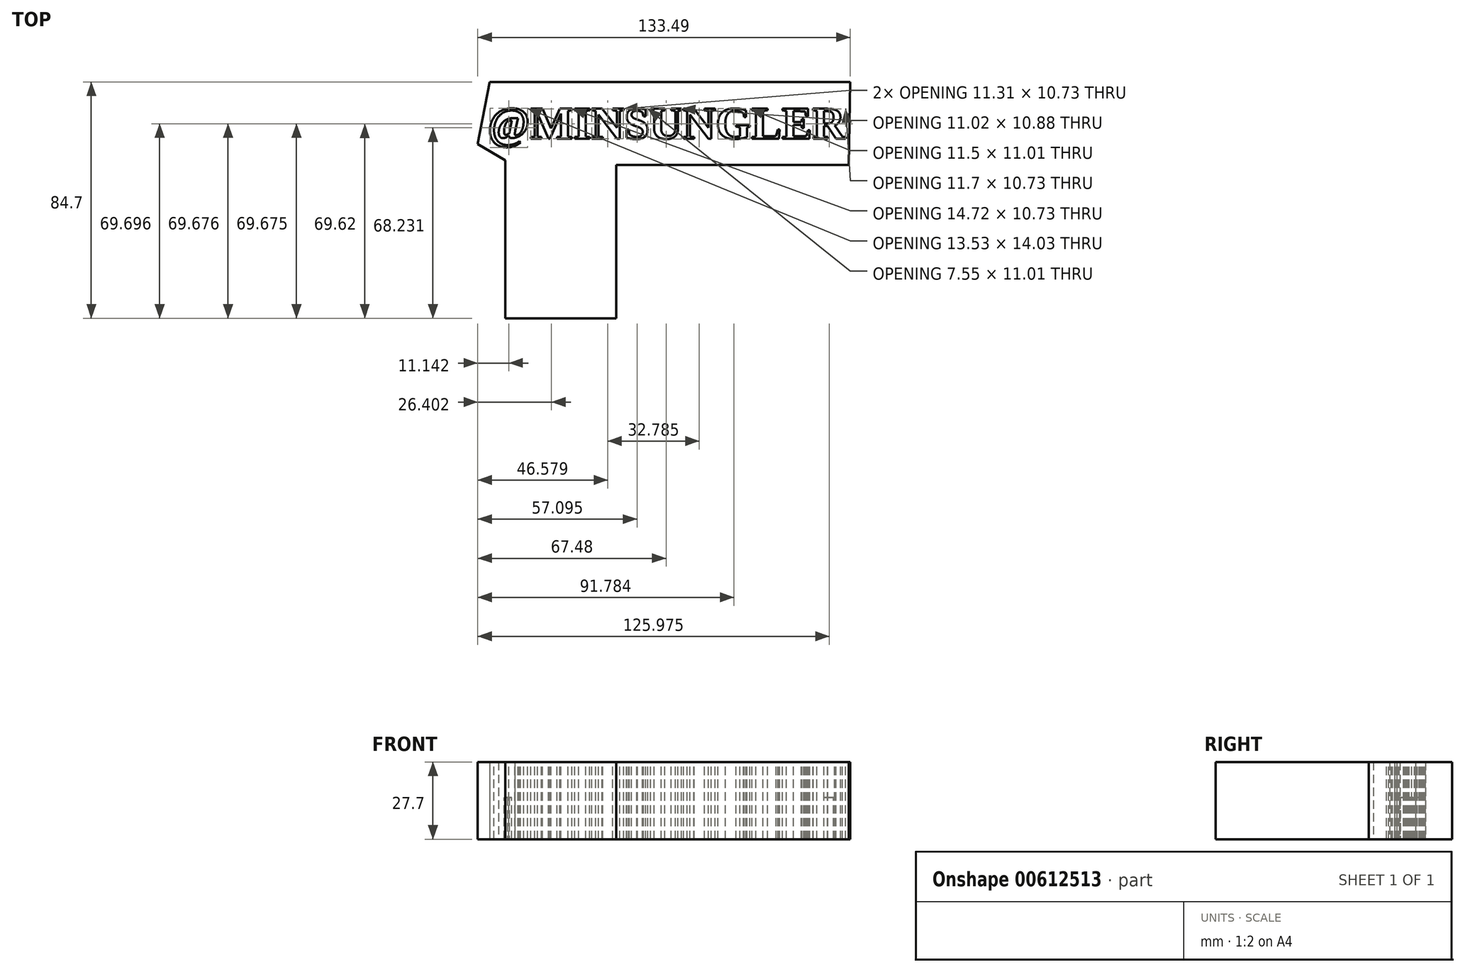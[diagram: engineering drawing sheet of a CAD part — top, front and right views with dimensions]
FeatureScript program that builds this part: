
annotation { "Feature Type Name" : "Feature", "Feature Type Description" : "" }
export const myFeature = defineFeature(function(context is Context, id is Id, definition is map)
    precondition{}
    {
        {
            var Q0;
            Q0=qCreatedBy(makeId("Top.planeOp"),FACE);
            var sketch = newSketch(context, id + "F0", { "sketchPlane" : qUnion([Q0])});
            skLineSegment(sketch, "E0", {"start": v(76.26, 48.78) * mm, "end": v(-52.94, 48.78) * mm});
            skLineSegment(sketch, "E1", {"start": v(-52.94, 48.78) * mm, "end": v(-57.23, 26.54) * mm});
            skLineSegment(sketch, "E2", {"start": v(-57.23, 26.54) * mm, "end": v(-47.3, 20.64) * mm});
            skLineSegment(sketch, "E3", {"start": v(-47.3, 20.64) * mm, "end": v(-47.3, -35.92) * mm});
            skLineSegment(sketch, "E4", {"start": v(-47.3, -35.92) * mm, "end": v(-7.64, -35.92) * mm});
            skLineSegment(sketch, "E5", {"start": v(-7.64, -35.92) * mm, "end": v(-7.64, 19.03) * mm});
            skLineSegment(sketch, "E6", {"start": v(-7.64, 19.03) * mm, "end": v(75.72, 19.03) * mm});
            skLineSegment(sketch, "E7", {"start": v(75.72, 19.03) * mm, "end": v(76.26, 48.78) * mm});
            skSolve(sketch);
        }
        {
            var Q0;
            Q0=makeQuery(id+"F0.imprint","IMPRINT",FACE,{"disambiguationData":[TD([[makeQuery(id+"F0.imprint","IMPRINT",EDGE,{"derivedFrom":sQuery(id+"F0.wireOp",EDGE,"E0")}),1.0]])]});
            extrude(context, id + "F1", {"entities" : qUnion([Q0]), "depth" : 15 * mm, "offsetDistance" : 25.4 * mm});
        }
        {
            var Q0;
            Q0=makeQuery(id+"F1.opExtrude","CAP_FACE",FACE,{"disambiguationData":[OSD([sQuery(id+"F0.wireOp",EDGE,"E0"),sQuery(id+"F0.wireOp",EDGE,"E1"),sQuery(id+"F0.wireOp",EDGE,"E2"),sQuery(id+"F0.wireOp",EDGE,"E3"),sQuery(id+"F0.wireOp",EDGE,"E4"),sQuery(id+"F0.wireOp",EDGE,"E5"),sQuery(id+"F0.wireOp",EDGE,"E6"),sQuery(id+"F0.wireOp",EDGE,"E7")])],"isStart":false});
            var sketch = newSketch(context, id + "F2", { "sketchPlane" : qUnion([Q0])});
            skText(sketch, "E8", { "text": "@MINSUNGLER", "fontName": "Tinos-Bold.ttf"});
            const initialGuessF2  = {"E8": [-0.05371, 0.02841, 1, 0, 0.0118]};
            skSetInitialGuess(sketch, initialGuessF2);
            skSolve(sketch);
        }
        {
            var Q0;
            Q0 = qSketchRegion(id + "F2", true);
            extrude(context, id + "F3", {"entities" : qUnion([Q0]), "operationType" : NewBodyOperationType.REMOVE, "oppositeDirection" : true, "depth" : 101.6 * mm, "offsetDistance" : 25.4 * mm});
        }
        {
            var Q0;
            {var subQ0=sQuery(id+"F0.wireOp",EDGE,"E2");var subQ1=sQuery(id+"F0.wireOp",EDGE,"E7");var subQ2=sQuery(id+"F0.wireOp",EDGE,"E6");var subQ3=sQuery(id+"F0.wireOp",EDGE,"E5");var subQ4=sQuery(id+"F0.wireOp",EDGE,"E4");var subQ5=sQuery(id+"F0.wireOp",EDGE,"E0");var subQ6=sQuery(id+"F0.wireOp",EDGE,"E3");var subQ7=sQuery(id+"F0.wireOp",EDGE,"E1");Q0=makeQuery(id+"F3.boolean.opBoolean","SPLIT",FACE,{"disambiguationData":[TD([makeQuery(id+"F1.opExtrude","SWEPT_FACE",FACE,{"disambiguationData":[OSD([subQ5])]})])],"derivedFrom":makeQuery(id+"F1.opExtrude","CAP_FACE",FACE,{"disambiguationData":[OSD([subQ5,subQ7,subQ0,subQ6,subQ4,subQ3,subQ2,subQ1])],"isStart":false})});}
            extrude(context, id + "F4", {"entities" : qUnion([Q0]), "operationType" : NewBodyOperationType.ADD, "depth" : 12.7 * mm, "offsetDistance" : 25.4 * mm});
        }
    });
